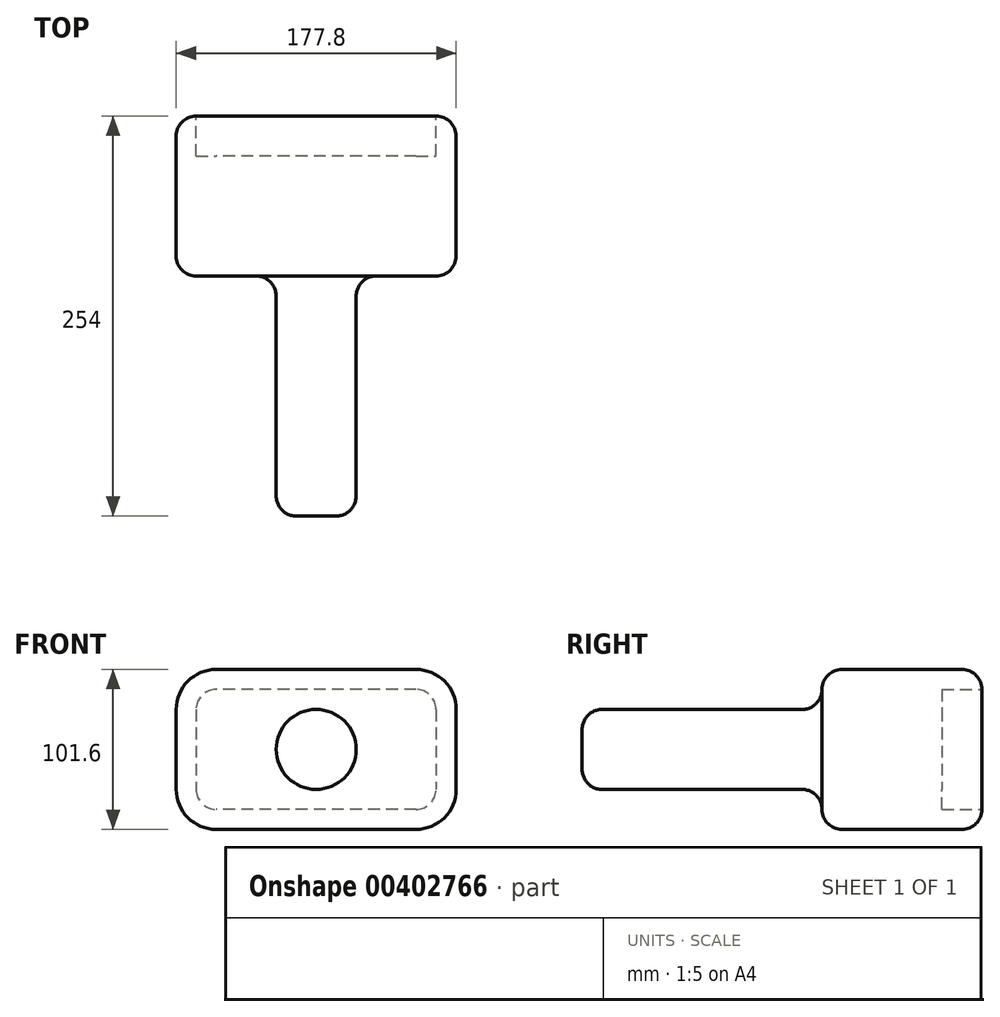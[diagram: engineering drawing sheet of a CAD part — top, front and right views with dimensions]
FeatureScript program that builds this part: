
annotation { "Feature Type Name" : "Feature", "Feature Type Description" : "" }
export const myFeature = defineFeature(function(context is Context, id is Id, definition is map)
    precondition{}
    {
        {
            var Q0;
            Q0=qCreatedBy(makeId("Front.planeOp"),FACE);
            var sketch = newSketch(context, id + "F0", { "sketchPlane" : qUnion([Q0])});
            skLineSegment(sketch, "E0.bottom", {"start": v(88.9, 50.8) * mm, "end": v(-88.9, 50.8) * mm});
            skLineSegment(sketch, "E0.top", {"start": v(88.9, -50.8) * mm, "end": v(-88.9, -50.8) * mm});
            skLineSegment(sketch, "E0.left", {"start": v(88.9, 50.8) * mm, "end": v(88.9, -50.8) * mm});
            skLineSegment(sketch, "E0.right", {"start": v(-88.9, 50.8) * mm, "end": v(-88.9, -50.8) * mm});
            skPoint(sketch, "E0.middle", {"position": v(0, 0) * mm});
            skSolve(sketch);
        }
        {
            var Q0;
            Q0=qCreatedBy(makeId("Front.planeOp"),FACE);
            var sketch = newSketch(context, id + "F1", { "sketchPlane" : qUnion([Q0])});
            skLineSegment(sketch, "E1.0", {"start": v(76.2, 38.1) * mm, "end": v(-76.2, 38.1) * mm});
            skLineSegment(sketch, "E1.1", {"start": v(76.2, 38.1) * mm, "end": v(76.2, -38.1) * mm});
            skLineSegment(sketch, "E1.2", {"start": v(76.2, -38.1) * mm, "end": v(-76.2, -38.1) * mm});
            skLineSegment(sketch, "E1.3", {"start": v(-76.2, 38.1) * mm, "end": v(-76.2, -38.1) * mm});
            skSolve(sketch);
        }
        {
            var Q0;
            Q0=qCreatedBy(makeId("Front.planeOp"),FACE);
            var sketch = newSketch(context, id + "F2", { "sketchPlane" : qUnion([Q0])});
            skCircle(sketch, "E2", {"center": v(0, 0) * mm, "radius": 25.4 * mm});
            skSolve(sketch);
        }
        {
            var Q0;
            Q0=makeQuery(id+"F0.imprint","IMPRINT",FACE,{"disambiguationData":[TD([[makeQuery(id+"F0.imprint","IMPRINT",EDGE,{"derivedFrom":sQuery(id+"F0.wireOp",EDGE,"E0.bottom")}),1.0]])]});
            extrude(context, id + "F3", {"entities" : qUnion([Q0]), "depth" : 101.6 * mm});
        }
        {
            var Q0;
            Q0=makeQuery(id+"F2.imprint","IMPRINT",FACE,{"disambiguationData":[TD([[makeQuery(id+"F2.imprint","IMPRINT",EDGE,{"derivedFrom":sQuery(id+"F2.wireOp",EDGE,"E2")}),1.0]])]});
            extrude(context, id + "F4", {"entities" : qUnion([Q0]), "operationType" : NewBodyOperationType.ADD, "depth" : 254 * mm, "offsetDistance" : 25.4 * mm});
        }
        {
            var Q0;
            Q0=makeQuery(id+"F1.imprint","IMPRINT",FACE,{"disambiguationData":[TD([[makeQuery(id+"F1.imprint","IMPRINT",EDGE,{"derivedFrom":sQuery(id+"F1.wireOp",EDGE,"E1.0")}),1.0]])]});
            extrude(context, id + "F5", {"entities" : qUnion([Q0]), "operationType" : NewBodyOperationType.REMOVE, "depth" : 25.4 * mm});
        }
        {
            var Q0;
            Q0=makeQuery(id+"F5.boolean.opBoolean","COPY",EDGE,{"derivedFrom":makeQuery(id+"F5.opExtrude","SWEPT_EDGE",EDGE,{"disambiguationData":[OSD([sQuery(id+"F1.wireOp",EDGE,"E1.2"),sQuery(id+"F1.wireOp",EDGE,"E1.3")])]})});
            var Q1;
            Q1=makeQuery(id+"F5.boolean.opBoolean","COPY",EDGE,{"derivedFrom":makeQuery(id+"F5.opExtrude","SWEPT_EDGE",EDGE,{"disambiguationData":[OSD([sQuery(id+"F1.wireOp",EDGE,"E1.0"),sQuery(id+"F1.wireOp",EDGE,"E1.3")])]})});
            var Q2;
            Q2=makeQuery(id+"F5.boolean.opBoolean","COPY",EDGE,{"derivedFrom":makeQuery(id+"F5.opExtrude","SWEPT_EDGE",EDGE,{"disambiguationData":[OSD([sQuery(id+"F1.wireOp",EDGE,"E1.0"),sQuery(id+"F1.wireOp",EDGE,"E1.1")])]})});
            var Q3;
            Q3=makeQuery(id+"F5.boolean.opBoolean","COPY",EDGE,{"derivedFrom":makeQuery(id+"F5.opExtrude","SWEPT_EDGE",EDGE,{"disambiguationData":[OSD([sQuery(id+"F1.wireOp",EDGE,"E1.1"),sQuery(id+"F1.wireOp",EDGE,"E1.2")])]})});
            fillet(context, id + "F6", {"entities" : qUnion([Q0, Q1, Q2, Q3]), "radius" : 12.7 * mm, "tangentPropagation" : true, "allowEdgeOverflow" : false});
        }
        {
            var Q0;
            Q0=makeQuery(id+"F3.opExtrude","SWEPT_EDGE",EDGE,{"disambiguationData":[OSD([sQuery(id+"F0.wireOp",EDGE,"E0.top"),sQuery(id+"F0.wireOp",EDGE,"E0.right")])]});
            var Q1;
            Q1=makeQuery(id+"F3.opExtrude","SWEPT_EDGE",EDGE,{"disambiguationData":[OSD([sQuery(id+"F0.wireOp",EDGE,"E0.top"),sQuery(id+"F0.wireOp",EDGE,"E0.left")])]});
            var Q2;
            Q2=makeQuery(id+"F3.opExtrude","SWEPT_EDGE",EDGE,{"disambiguationData":[OSD([sQuery(id+"F0.wireOp",EDGE,"E0.bottom"),sQuery(id+"F0.wireOp",EDGE,"E0.right")])]});
            var Q3;
            Q3=makeQuery(id+"F3.opExtrude","SWEPT_EDGE",EDGE,{"disambiguationData":[OSD([sQuery(id+"F0.wireOp",EDGE,"E0.bottom"),sQuery(id+"F0.wireOp",EDGE,"E0.left")])]});
            fillet(context, id + "F7", {"entities" : qUnion([Q0, Q1, Q2, Q3]), "radius" : 25.4 * mm, "tangentPropagation" : true, "allowEdgeOverflow" : false});
        }
        {
            var Q0;
            Q0=makeQuery(id+"F3.opExtrude","CAP_EDGE",EDGE,{"disambiguationData":[OSD([sQuery(id+"F0.wireOp",EDGE,"E0.left")])],"isStart":false});
            var Q1;
            Q1=makeQuery(id+"F4.opExtrude","CAP_EDGE",EDGE,{"disambiguationData":[OSD([sQuery(id+"F2.wireOp",EDGE,"E2")])],"isStart":false});
            var Q2;
            Q2=makeQuery(id+"F4.boolean.opBoolean","INTERSECT",EDGE,{"derivedFrom":[makeQuery(id+"F3.opExtrude","CAP_FACE",FACE,{"disambiguationData":[OSD([sQuery(id+"F0.wireOp",EDGE,"E0.bottom"),sQuery(id+"F0.wireOp",EDGE,"E0.top"),sQuery(id+"F0.wireOp",EDGE,"E0.left"),sQuery(id+"F0.wireOp",EDGE,"E0.right")])],"isStart":false}),makeQuery(id+"F4.opExtrude","SWEPT_FACE",FACE,{"disambiguationData":[OSD([sQuery(id+"F2.wireOp",EDGE,"E2")])]})]});
            fillet(context, id + "F8", {"entities" : qUnion([Q0, Q1, Q2]), "radius" : 12.7 * mm, "tangentPropagation" : true, "allowEdgeOverflow" : false});
        }
        {
            var Q0;
            {var subQ0=sQuery(id+"F0.wireOp",EDGE,"E0.right");var subQ1=sQuery(id+"F0.wireOp",EDGE,"E0.top");Q0=makeQuery(id+"F7.opFillet","BLEND_EDGE",EDGE,{"blendedFrom":[makeQuery(id+"F3.opExtrude","SWEPT_EDGE",EDGE,{"disambiguationData":[OSD([subQ1,subQ0])]}),makeQuery(id+"F3.opExtrude","CAP_FACE",FACE,{"disambiguationData":[OSD([sQuery(id+"F0.wireOp",EDGE,"E0.bottom"),subQ1,sQuery(id+"F0.wireOp",EDGE,"E0.left"),subQ0])],"isStart":true})],"blendedInto":[makeQuery(id+"F3.opExtrude","CAP_FACE",FACE,{"disambiguationData":[OSD([sQuery(id+"F0.wireOp",EDGE,"E0.bottom"),subQ1,sQuery(id+"F0.wireOp",EDGE,"E0.left"),subQ0])],"isStart":true})]});}
            fillet(context, id + "F9", {"entities" : qUnion([Q0]), "radius" : 12.7 * mm, "tangentPropagation" : true, "allowEdgeOverflow" : false});
        }
    });
